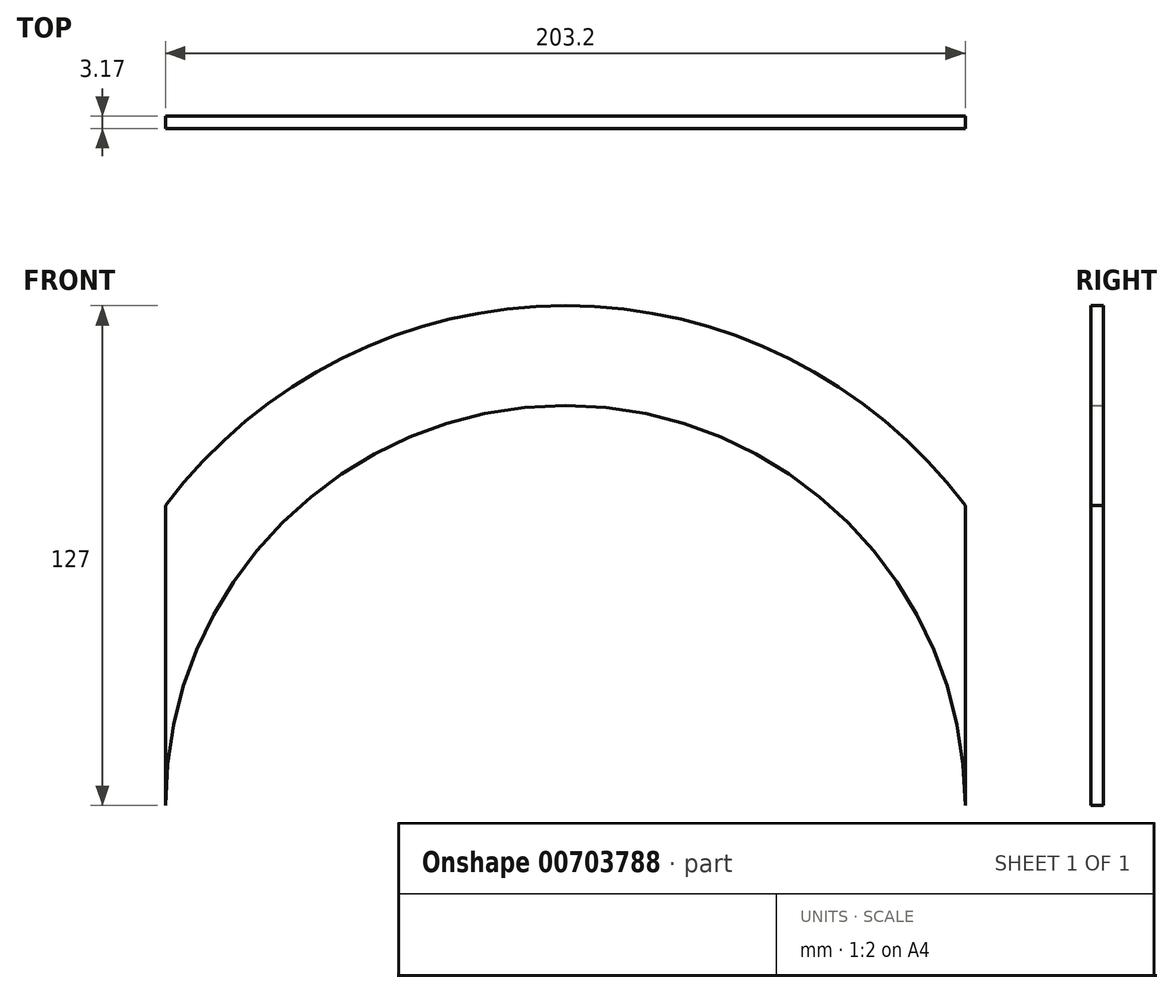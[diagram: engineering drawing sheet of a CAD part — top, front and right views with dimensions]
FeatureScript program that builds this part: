
annotation { "Feature Type Name" : "Feature", "Feature Type Description" : "" }
export const myFeature = defineFeature(function(context is Context, id is Id, definition is map)
    precondition{}
    {
        {
            var Q0;
            Q0=qCreatedBy(makeId("Front.planeOp"),FACE);
            var sketch = newSketch(context, id + "F0", { "sketchPlane" : qUnion([Q0])});
            skArc(sketch, "E0", {"start": v(101.6, 0) * mm, "mid": v(0, 101.6) * mm, "end": v(-101.6, 0) * mm});
            skArc(sketch, "E1", {"start": v(101.6, 76.2) * mm, "mid": v(0, 127) * mm, "end": v(-101.6, 76.2) * mm});
            skLineSegment(sketch, "E2", {"start": v(101.6, 0) * mm, "end": v(101.6, 76.2) * mm});
            skLineSegment(sketch, "E3", {"start": v(-101.6, 0) * mm, "end": v(-101.6, 76.2) * mm});
            skSolve(sketch);
        }
        {
            var Q0;
            Q0=makeQuery(id+"F0.imprint","IMPRINT",FACE,{"disambiguationData":[TD([[makeQuery(id+"F0.imprint","IMPRINT",EDGE,{"derivedFrom":sQuery(id+"F0.wireOp",EDGE,"E0")}),-1.0]])]});
            extrude(context, id + "F1", {"entities" : qUnion([Q0]), "depth" : 3.17 * mm, "offsetDistance" : 25.4 * mm});
        }
    });
